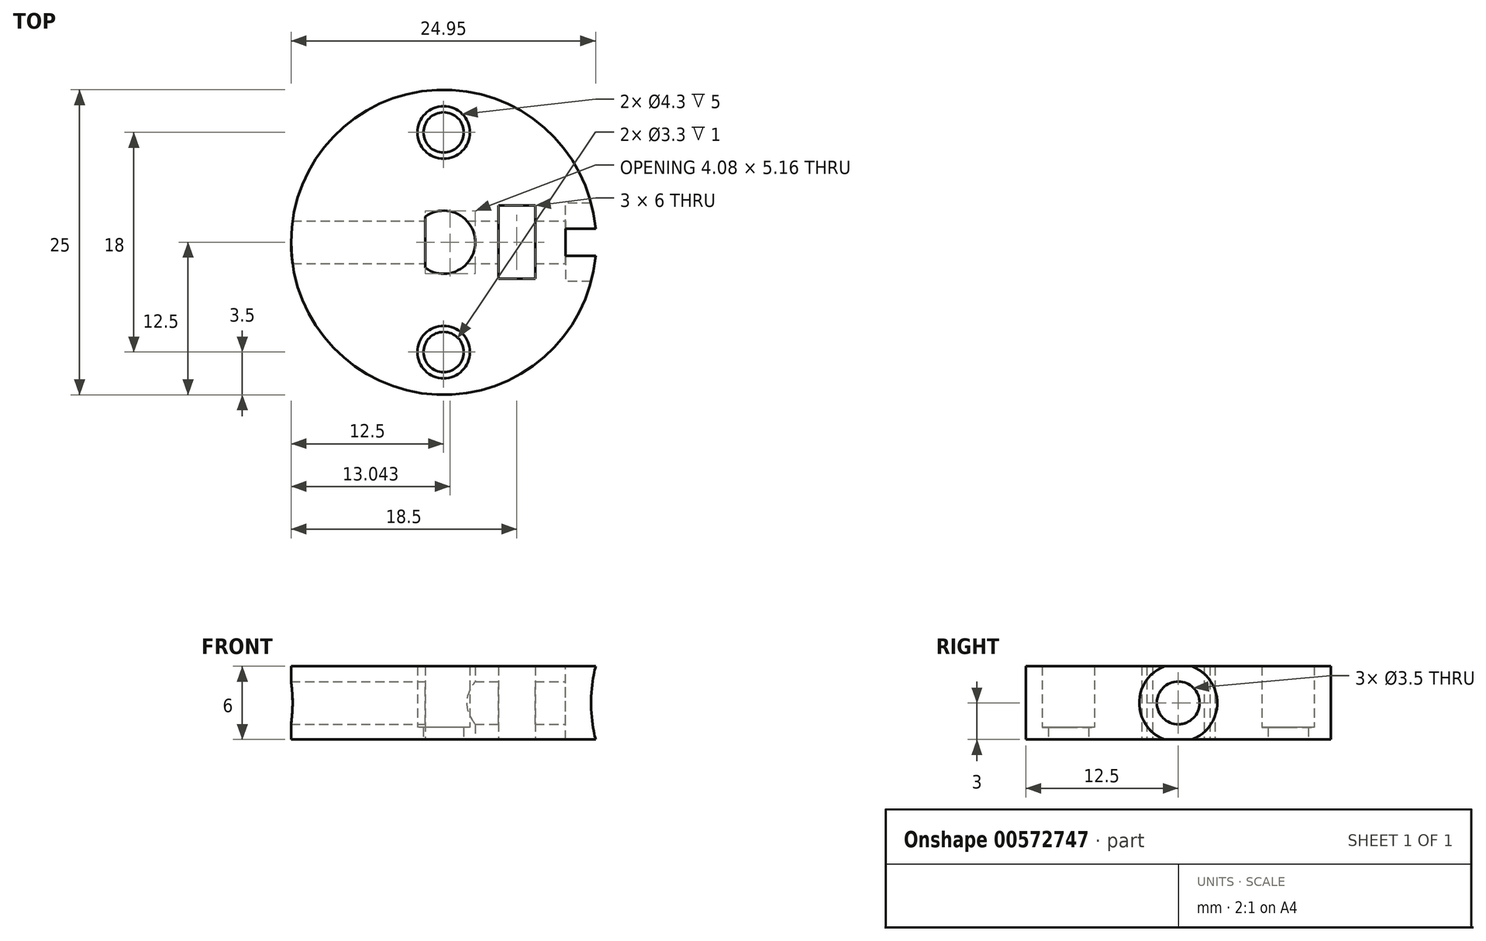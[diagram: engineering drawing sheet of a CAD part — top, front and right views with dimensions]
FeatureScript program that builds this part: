
annotation { "Feature Type Name" : "Feature", "Feature Type Description" : "" }
export const myFeature = defineFeature(function(context is Context, id is Id, definition is map)
    precondition{}
    {
        {
            var Q0;
            Q0=qCreatedBy(makeId("Top.planeOp"),FACE);
            var sketch = newSketch(context, id + "F0", { "sketchPlane" : qUnion([Q0])});
            skCircle(sketch, "E0", {"center": v(0, 0) * mm, "radius": 12.5 * mm});
            skCircle(sketch, "E1", {"center": v(0, 0) * mm, "radius": 2.58 * mm});
            skCircle(sketch, "E2", {"center": v(0, 9) * mm, "radius": 1.65 * mm});
            skCircle(sketch, "E3", {"center": v(0, -9) * mm, "radius": 1.65 * mm});
            skCircle(sketch, "E4", {"center": v(0, 9) * mm, "radius": 2.15 * mm});
            skCircle(sketch, "E5", {"center": v(0, -9) * mm, "radius": 2.15 * mm});
            skLineSegment(sketch, "E6.bottom", {"start": v(7.5, 3) * mm, "end": v(4.5, 3) * mm});
            skLineSegment(sketch, "E6.top", {"start": v(7.5, -3) * mm, "end": v(4.5, -3) * mm});
            skLineSegment(sketch, "E6.left", {"start": v(7.5, 3) * mm, "end": v(7.5, -3) * mm});
            skLineSegment(sketch, "E6.right", {"start": v(4.5, 3) * mm, "end": v(4.5, -3) * mm});
            skPoint(sketch, "E6.middle", {"position": v(6, 0) * mm});
            skLineSegment(sketch, "E7", {"start": v(-1.5, 2.1) * mm, "end": v(-1.5, -2.1) * mm});
            skSolve(sketch);
        }
        {
            var Q0;
            Q0=qSketchRegion(id+"F0",true);
            var Q1;
            Q1=makeQuery(id+"F0.imprint","IMPRINT",FACE,{"disambiguationData":[TD([[makeQuery(id+"F0.imprint","IMPRINT",EDGE,{"derivedFrom":sQuery(id+"F0.wireOp",EDGE,"E0")}),1.0]])]});
            var Q2;
            {var subQ0=sQuery(id+"F0.wireOp",EDGE,"E7");Q2=makeQuery(id+"F0.imprint","IMPRINT",FACE,{"disambiguationData":[TD([[makeQuery(id+"F0.imprint","IMPRINT",EDGE,{"derivedFrom":subQ0}),-1.0]])]});}
            extrude(context, id + "F1", {"entities" : qUnion([Q0, Q1, Q2]), "depth" : 6 * mm, "offsetDistance" : 25 * mm});
        }
        {
            var Q0;
            Q0=makeQuery(id+"F0.imprint","IMPRINT",FACE,{"disambiguationData":[TD([[makeQuery(id+"F0.imprint","IMPRINT",EDGE,{"derivedFrom":sQuery(id+"F0.wireOp",EDGE,"E2")}),-1.0]])]});
            var Q1;
            Q1=makeQuery(id+"F0.imprint","IMPRINT",FACE,{"disambiguationData":[TD([[makeQuery(id+"F0.imprint","IMPRINT",EDGE,{"derivedFrom":sQuery(id+"F0.wireOp",EDGE,"E3")}),-1.0]])]});
            extrude(context, id + "F2", {"entities" : qUnion([Q0, Q1]), "operationType" : NewBodyOperationType.ADD, "depth" : 1 * mm, "offsetDistance" : 25 * mm});
        }
        {
            var Q0;
            Q0=qCreatedBy(makeId("Right.planeOp"),FACE);
            var sketch = newSketch(context, id + "F3", { "sketchPlane" : qUnion([Q0])});
            skCircle(sketch, "E8", {"center": v(0, 3) * mm, "radius": 1.75 * mm});
            skCircle(sketch, "E9", {"center": v(0, 3) * mm, "radius": 3.2 * mm});
            skSolve(sketch);
        }
        {
            var Q0;
            Q0=makeQuery(id+"F3.imprint","IMPRINT",FACE,{"disambiguationData":[TD([[makeQuery(id+"F3.imprint","IMPRINT",EDGE,{"derivedFrom":sQuery(id+"F3.wireOp",EDGE,"E8")}),1.0]])]});
            extrude(context, id + "F4", {"entities" : qUnion([Q0]), "operationType" : NewBodyOperationType.REMOVE, "endBound" : BoundingType.SYMMETRIC, "oppositeDirection" : true, "depth" : 25 * mm, "offsetDistance" : 25 * mm});
        }
        {
            var Q0;
            Q0=makeQuery(id+"F3.imprint","IMPRINT",FACE,{"disambiguationData":[TD([[makeQuery(id+"F3.imprint","IMPRINT",EDGE,{"derivedFrom":sQuery(id+"F3.wireOp",EDGE,"E8")}),-1.0]])]});
            extrude(context, id + "F5", {"entities" : qUnion([Q0]), "operationType" : NewBodyOperationType.REMOVE, "depth" : 25 * mm, "offsetDistance" : 25 * mm, "hasSecondDirection" : true, "secondDirectionOppositeDirection" : false, "secondDirectionDepth" : 10 * mm});
        }
    });
